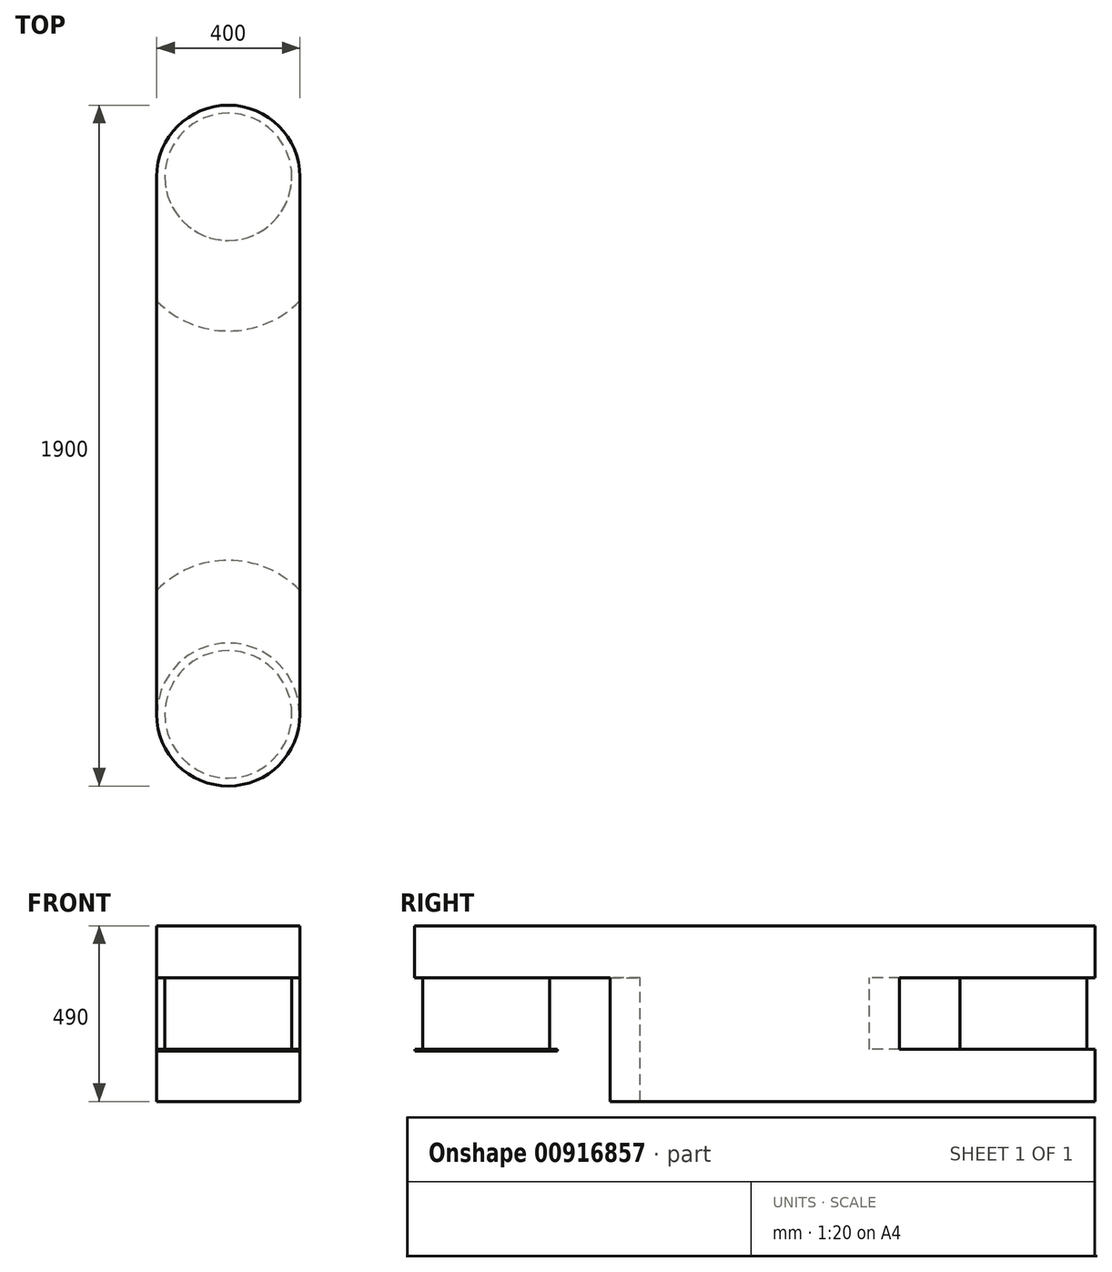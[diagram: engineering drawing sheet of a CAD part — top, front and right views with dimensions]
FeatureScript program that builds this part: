
annotation { "Feature Type Name" : "Feature", "Feature Type Description" : "" }
export const myFeature = defineFeature(function(context is Context, id is Id, definition is map)
    precondition{}
    {
        {
            var Q0;
            Q0=qCreatedBy(makeId("Top.planeOp"),FACE);
            var sketch = newSketch(context, id + "F0", { "sketchPlane" : qUnion([Q0])});
            skLineSegment(sketch, "E0.bottom", {"start": v(-200, 750) * mm, "end": v(200, 750) * mm});
            skLineSegment(sketch, "E0.top", {"start": v(-200, -750) * mm, "end": v(200, -750) * mm});
            skLineSegment(sketch, "E0.left", {"start": v(-200, 750) * mm, "end": v(-200, -750) * mm});
            skLineSegment(sketch, "E0.right", {"start": v(200, 750) * mm, "end": v(200, -750) * mm});
            skPoint(sketch, "E0.middle", {"position": v(0, 0) * mm});
            skArc(sketch, "E1", {"start": v(200, 750) * mm, "mid": v(0, 950) * mm, "end": v(-200, 750) * mm});
            skArc(sketch, "E2", {"start": v(-200, -750) * mm, "mid": v(0, -950) * mm, "end": v(200, -750) * mm});
            skSolve(sketch);
        }
        {
            var Q0;
            Q0=qSketchRegion(id+"F0",true);
            extrude(context, id + "F1", {"entities" : qUnion([Q0]), "depth" : 145 * mm, "offsetDistance" : 25 * mm});
        }
        {
            var Q0;
            Q0=makeQuery(id+"F1.opExtrude","CAP_FACE",FACE,{"disambiguationData":[OSD([sQuery(id+"F0.wireOp",EDGE,"E0.left"),sQuery(id+"F0.wireOp",EDGE,"E0.right"),sQuery(id+"F0.wireOp",EDGE,"E1"),sQuery(id+"F0.wireOp",EDGE,"E2")])],"isStart":true});
            var sketch = newSketch(context, id + "F2", { "sketchPlane" : qUnion([Q0])});
            skCircle(sketch, "E3", {"center": v(0, 750) * mm, "radius": 177.5 * mm});
            skCircle(sketch, "E4", {"center": v(0, -750) * mm, "radius": 177.5 * mm});
            skArc(sketch, "E5", {"start": v(-200, 404.04) * mm, "mid": v(0.03, 320.08) * mm, "end": v(200, 404.2) * mm});
            skArc(sketch, "E6", {"start": v(200, -404.04) * mm, "mid": v(0, -320) * mm, "end": v(-200, -404.04) * mm});
            skSolve(sketch);
        }
        {
            var Q0;
            Q0=qSketchRegion(id+"F2",true);
            var Q1;
            {var subQ0=sQuery(id+"F2.wireOp",EDGE,"E5");Q1=makeQuery(id+"F2.imprint","IMPRINT",FACE,{"disambiguationData":[TD([[makeQuery(id+"F2.imprint","IMPRINT",EDGE,{"derivedFrom":subQ0}),-1.0]])]});}
            extrude(context, id + "F3", {"entities" : qUnion([Q0, Q1]), "operationType" : NewBodyOperationType.ADD, "depth" : 200 * mm, "offsetDistance" : 25 * mm});
        }
        {
            var Q0;
            Q0=makeQuery(id+"F3.opExtrude","CAP_FACE",FACE,{"disambiguationData":[OSD([sQuery(id+"F0.wireOp",EDGE,"E0.left"),sQuery(id+"F0.wireOp",EDGE,"E0.right"),sQuery(id+"F2.wireOp",EDGE,"E5"),sQuery(id+"F2.wireOp",EDGE,"E6")])],"isStart":false});
            var sketch = newSketch(context, id + "F4", { "sketchPlane" : qUnion([Q0])});
            skLineSegment(sketch, "E7.top", {"start": v(-200, -750) * mm, "end": v(200, -750) * mm});
            skLineSegment(sketch, "E7.left", {"start": v(-200, 404.04) * mm, "end": v(-200, -750) * mm});
            skLineSegment(sketch, "E7.right", {"start": v(200, 404.2) * mm, "end": v(200, -750) * mm});
            skPoint(sketch, "E7.middle", {"position": v(0, 0) * mm});
            skArc(sketch, "E8", {"start": v(-200, -750) * mm, "mid": v(0, -950) * mm, "end": v(200, -750) * mm});
            skArc(sketch, "E9", {"start": v(-200, 404.04) * mm, "mid": v(0.03, 320.08) * mm, "end": v(200, 404.2) * mm});
            skSolve(sketch);
        }
        {
            var Q0;
            Q0 = qSketchRegion(id + "F4", true);
            extrude(context, id + "F5", {"entities" : qUnion([Q0]), "operationType" : NewBodyOperationType.ADD, "depth" : 145 * mm, "offsetDistance" : 25 * mm});
        }
        {
            var Q0;
            Q0=makeQuery(id+"F3.opExtrude","CAP_FACE",FACE,{"disambiguationData":[OSD([sQuery(id+"F2.wireOp",EDGE,"E3")])],"isStart":false});
            var sketch = newSketch(context, id + "F6", { "sketchPlane" : qUnion([Q0])});
            skCircle(sketch, "E10", {"center": v(0, 750) * mm, "radius": 199 * mm});
            skSolve(sketch);
        }
        {
            var Q0;
            Q0 = qSketchRegion(id + "F6", true);
            extrude(context, id + "F7", {"entities" : qUnion([Q0]), "operationType" : NewBodyOperationType.ADD, "depth" : 5 * mm, "offsetDistance" : 25 * mm});
        }
    });
